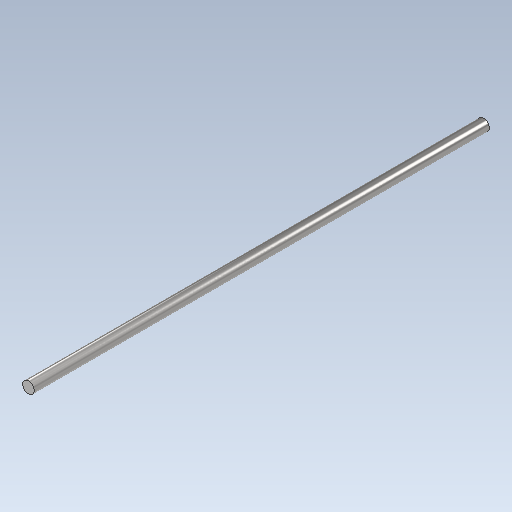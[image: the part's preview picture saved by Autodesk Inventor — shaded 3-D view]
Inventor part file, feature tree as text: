
AUTODESK INVENTOR PART (.ipt)
format: ipt  version: 2020 (Build 240168000, 168)  size: 92,160 bytes
history: native  units: mm
features: other x4, extrude x1, sketch x1, reference x1
ambient origin geometry x8: Origin, YZ Plane, XZ Plane, XY Plane, X Axis, Y Axis, Z Axis, Center Point
bodies: Body1 (feature_tree)
feature tree (7):
  other  "Bryła1"
  extrude  "Wyciągnięcie proste1"  Depth=100.0mm TaperAngle=0.0deg
  sketch  "Szkic1"
  reference  "Odniesienie1"
  other  "<userpath>\Desktop\3d\scanning-robot\Assembly1.iam"
  other  "Assembly1.iam"
  other  "wheel-adapter:1"
